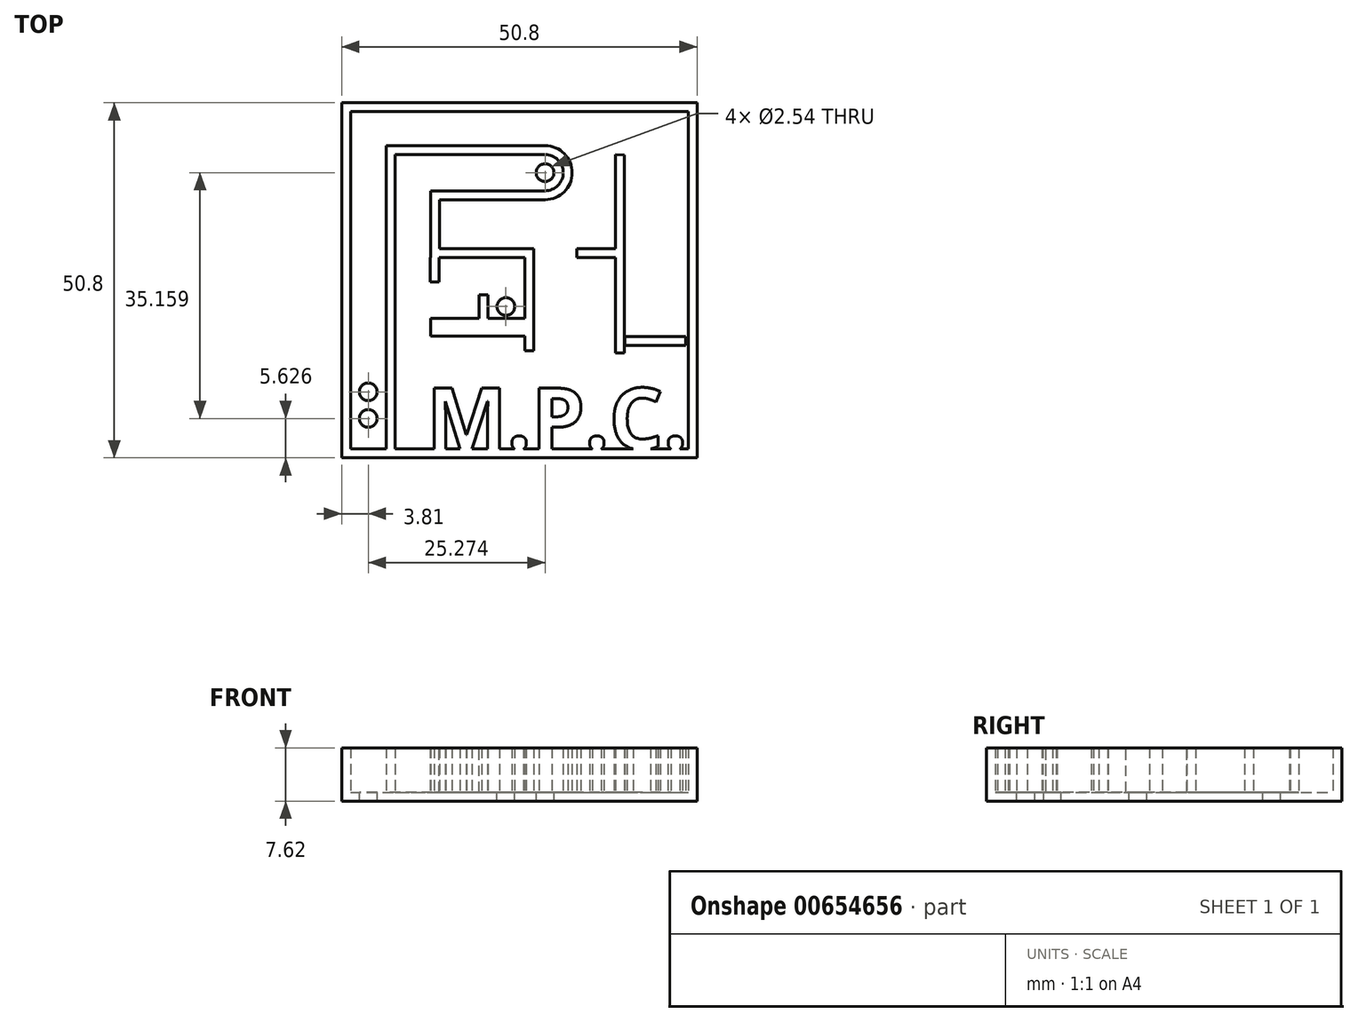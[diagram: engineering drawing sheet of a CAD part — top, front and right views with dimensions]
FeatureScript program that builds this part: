
annotation { "Feature Type Name" : "Feature", "Feature Type Description" : "" }
export const myFeature = defineFeature(function(context is Context, id is Id, definition is map)
    precondition{}
    {
        {
            var Q0;
            Q0=qCreatedBy(makeId("Top.planeOp"),FACE);
            var sketch = newSketch(context, id + "F0", { "sketchPlane" : qUnion([Q0])});
            skLineSegment(sketch, "E0.bottom", {"start": v(0, 0) * mm, "end": v(50.8, 0) * mm});
            skLineSegment(sketch, "E0.top", {"start": v(0, 50.8) * mm, "end": v(50.8, 50.8) * mm});
            skLineSegment(sketch, "E0.left", {"start": v(0, 0) * mm, "end": v(0, 50.8) * mm});
            skLineSegment(sketch, "E0.right", {"start": v(50.8, 0) * mm, "end": v(50.8, 50.8) * mm});
            skSolve(sketch);
        }
        {
            var Q0;
            Q0 = qSketchRegion(id + "F0", true);
            extrude(context, id + "F1", {"entities" : qUnion([Q0]), "depth" : 7.62 * mm, "offsetDistance" : 25.4 * mm});
        }
        {
            var Q0;
            Q0=makeQuery(id+"F1.opExtrude","CAP_FACE",FACE,{"disambiguationData":[OSD([sQuery(id+"F0.wireOp",EDGE,"E0.bottom"),sQuery(id+"F0.wireOp",EDGE,"E0.top"),sQuery(id+"F0.wireOp",EDGE,"E0.left"),sQuery(id+"F0.wireOp",EDGE,"E0.right")])],"isStart":false});
            shell(context, id + "F2", {"entities" : qUnion([Q0]), "thickness" : 1.27 * mm});
        }
        {
            var Q0;
            Q0=makeQuery(id+"F2.opShell","OFFSET_FACE",FACE,{"disambiguationData":[OSD([sQuery(id+"F0.wireOp",EDGE,"E0.bottom"),sQuery(id+"F0.wireOp",EDGE,"E0.top"),sQuery(id+"F0.wireOp",EDGE,"E0.left"),sQuery(id+"F0.wireOp",EDGE,"E0.right")])]});
            var sketch = newSketch(context, id + "F3", { "sketchPlane" : qUnion([Q0])});
            skLineSegment(sketch, "E1", {"start": v(1.27, 5.76) * mm, "end": v(6.35, 5.76) * mm});
            skLineSegment(sketch, "E2", {"start": v(6.35, 5.76) * mm, "end": v(6.35, 1.27) * mm});
            skLineSegment(sketch, "E3", {"start": v(6.35, 1.27) * mm, "end": v(7.62, 1.27) * mm});
            skLineSegment(sketch, "E4", {"start": v(7.62, 1.27) * mm, "end": v(7.62, 44.65) * mm});
            skLineSegment(sketch, "E5", {"start": v(7.62, 44.65) * mm, "end": v(6.35, 44.65) * mm});
            skLineSegment(sketch, "E6", {"start": v(6.35, 44.65) * mm, "end": v(6.35, 5.76) * mm});
            skSolve(sketch);
        }
        {
            var Q0;
            Q0=makeQuery(id+"F3.imprint","IMPRINT",FACE,{"disambiguationData":[TD([[makeQuery(id+"F3.imprint","IMPRINT",EDGE,{"derivedFrom":sQuery(id+"F3.wireOp",EDGE,"E2")}),1.0]])]});
            extrude(context, id + "F4", {"entities" : qUnion([Q0]), "operationType" : NewBodyOperationType.ADD, "depth" : 6.35 * mm, "offsetDistance" : 25.4 * mm});
        }
        {
            var Q0;
            Q0=makeQuery(id+"F2.opShell","OFFSET_FACE",FACE,{"disambiguationData":[OSD([sQuery(id+"F0.wireOp",EDGE,"E0.bottom"),sQuery(id+"F0.wireOp",EDGE,"E0.top"),sQuery(id+"F0.wireOp",EDGE,"E0.left"),sQuery(id+"F0.wireOp",EDGE,"E0.right")])]});
            var sketch = newSketch(context, id + "F5", { "sketchPlane" : qUnion([Q0])});
            skText(sketch, "E7", { "text": "M.P.C.", "fontName": "OpenSans-Bold.ttf"});
            const initialGuessF5  = {"E7": [0.01217, 0.00127, 1, 0, 0.00876]};
            skSetInitialGuess(sketch, initialGuessF5);
            skSolve(sketch);
        }
        {
            var Q0;
            Q0 = qSketchRegion(id + "F5", true);
            extrude(context, id + "F6", {"entities" : qUnion([Q0]), "operationType" : NewBodyOperationType.ADD, "depth" : 6.35 * mm, "offsetDistance" : 25.4 * mm});
        }
        {
            var Q0;
            {var subQ0=sQuery(id+"F0.wireOp",EDGE,"E0.top");var subQ1=sQuery(id+"F0.wireOp",EDGE,"E0.bottom");var subQ2=sQuery(id+"F0.wireOp",EDGE,"E0.right");var subQ3=sQuery(id+"F0.wireOp",EDGE,"E0.left");Q0=makeQuery(id+"F6.boolean.opBoolean","SPLIT",FACE,{"disambiguationData":[TD([makeQuery(id+"F2.opShell","OFFSET_FACE",FACE,{"disambiguationData":[OSD([subQ0])]})])],"derivedFrom":makeQuery(id+"F2.opShell","OFFSET_FACE",FACE,{"disambiguationData":[OSD([subQ1,subQ0,subQ3,subQ2])]})});}
            var sketch = newSketch(context, id + "F7", { "sketchPlane" : qUnion([Q0])});
            skCircle(sketch, "E8", {"center": v(3.81, 5.63) * mm, "radius": 1.27 * mm});
            skSolve(sketch);
        }
        {
            var Q0;
            Q0=makeQuery(id+"F7.imprint","IMPRINT",FACE,{"disambiguationData":[TD([[makeQuery(id+"F7.imprint","IMPRINT",EDGE,{"derivedFrom":sQuery(id+"F7.wireOp",EDGE,"E8")}),1.0]])]});
            extrude(context, id + "F8", {"entities" : qUnion([Q0]), "operationType" : NewBodyOperationType.REMOVE, "oppositeDirection" : true, "depth" : 7.62 * mm, "offsetDistance" : 25.4 * mm});
        }
        {
            var Q0;
            {var subQ0=sQuery(id+"F0.wireOp",EDGE,"E0.top");var subQ1=sQuery(id+"F0.wireOp",EDGE,"E0.bottom");var subQ2=sQuery(id+"F0.wireOp",EDGE,"E0.right");var subQ3=sQuery(id+"F0.wireOp",EDGE,"E0.left");Q0=makeQuery(id+"F6.boolean.opBoolean","SPLIT",FACE,{"disambiguationData":[TD([makeQuery(id+"F2.opShell","OFFSET_FACE",FACE,{"disambiguationData":[OSD([subQ0])]})])],"derivedFrom":makeQuery(id+"F2.opShell","OFFSET_FACE",FACE,{"disambiguationData":[OSD([subQ1,subQ0,subQ3,subQ2])]})});}
            var sketch = newSketch(context, id + "F9", { "sketchPlane" : qUnion([Q0])});
            skCircle(sketch, "E9", {"center": v(3.81, 9.44) * mm, "radius": 1.27 * mm});
            skSolve(sketch);
        }
        {
            var Q0;
            Q0=makeQuery(id+"F9.imprint","IMPRINT",FACE,{"disambiguationData":[TD([[makeQuery(id+"F9.imprint","IMPRINT",EDGE,{"derivedFrom":sQuery(id+"F9.wireOp",EDGE,"E9")}),1.0]])]});
            extrude(context, id + "F10", {"entities" : qUnion([Q0]), "operationType" : NewBodyOperationType.REMOVE, "oppositeDirection" : true, "depth" : 7.62 * mm, "offsetDistance" : 25.4 * mm});
        }
        {
            var Q0;
            {var subQ0=sQuery(id+"F0.wireOp",EDGE,"E0.top");var subQ1=sQuery(id+"F0.wireOp",EDGE,"E0.bottom");var subQ2=sQuery(id+"F0.wireOp",EDGE,"E0.right");var subQ3=sQuery(id+"F0.wireOp",EDGE,"E0.left");Q0=makeQuery(id+"F6.boolean.opBoolean","SPLIT",FACE,{"disambiguationData":[TD([makeQuery(id+"F2.opShell","OFFSET_FACE",FACE,{"disambiguationData":[OSD([subQ0])]})])],"derivedFrom":makeQuery(id+"F2.opShell","OFFSET_FACE",FACE,{"disambiguationData":[OSD([subQ1,subQ0,subQ3,subQ2])]})});}
            var sketch = newSketch(context, id + "F11", { "sketchPlane" : qUnion([Q0])});
            skLineSegment(sketch, "E10", {"start": v(7.62, 44.65) * mm, "end": v(29.08, 44.65) * mm});
            skLineSegment(sketch, "E11", {"start": v(29.08, 44.65) * mm, "end": v(29.08, 43.38) * mm});
            skLineSegment(sketch, "E12", {"start": v(29.08, 43.38) * mm, "end": v(7.62, 43.38) * mm});
            skLineSegment(sketch, "E13", {"start": v(7.62, 43.38) * mm, "end": v(7.62, 44.65) * mm});
            skArc(sketch, "E14", {"start": v(29.08, 38.2) * mm, "mid": v(31.68, 40.78) * mm, "end": v(29.08, 43.38) * mm});
            skLineSegment(sketch, "E15", {"start": v(29.08, 38.2) * mm, "end": v(29.08, 36.92) * mm});
            skArc(sketch, "E16", {"start": v(29.08, 36.92) * mm, "mid": v(32.95, 40.78) * mm, "end": v(29.08, 44.65) * mm});
            skSolve(sketch);
        }
        {
            var Q0;
            Q0 = qSketchRegion(id + "F11", true);
            extrude(context, id + "F12", {"entities" : qUnion([Q0]), "operationType" : NewBodyOperationType.ADD, "depth" : 6.35 * mm, "offsetDistance" : 25.4 * mm});
        }
        {
            var Q0;
            {var subQ0=sQuery(id+"F0.wireOp",EDGE,"E0.top");var subQ1=sQuery(id+"F0.wireOp",EDGE,"E0.bottom");var subQ2=sQuery(id+"F0.wireOp",EDGE,"E0.right");var subQ3=sQuery(id+"F0.wireOp",EDGE,"E0.left");Q0=makeQuery(id+"F6.boolean.opBoolean","SPLIT",FACE,{"disambiguationData":[TD([makeQuery(id+"F2.opShell","OFFSET_FACE",FACE,{"disambiguationData":[OSD([subQ0])]})])],"derivedFrom":makeQuery(id+"F2.opShell","OFFSET_FACE",FACE,{"disambiguationData":[OSD([subQ1,subQ0,subQ3,subQ2])]})});}
            var sketch = newSketch(context, id + "F13", { "sketchPlane" : qUnion([Q0])});
            skLineSegment(sketch, "E17", {"start": v(29.08, 38.2) * mm, "end": v(12.7, 38.2) * mm});
            skLineSegment(sketch, "E18", {"start": v(12.7, 38.2) * mm, "end": v(12.7, 36.92) * mm});
            skLineSegment(sketch, "E19", {"start": v(12.7, 36.92) * mm, "end": v(29.08, 36.92) * mm});
            skLineSegment(sketch, "E20", {"start": v(29.08, 36.92) * mm, "end": v(29.08, 38.2) * mm});
            skLineSegment(sketch, "E21", {"start": v(14.01, 38.2) * mm, "end": v(14.01, 38.3) * mm});
            skLineSegment(sketch, "E22", {"start": v(14.01, 38.3) * mm, "end": v(15.18, 38.3) * mm});
            skLineSegment(sketch, "E23", {"start": v(15.18, 38.3) * mm, "end": v(15.18, 38.2) * mm});
            skLineSegment(sketch, "E24", {"start": v(15.18, 38.2) * mm, "end": v(14.01, 38.2) * mm});
            skSolve(sketch);
        }
        {
            var Q0;
            {var subQ0=sQuery(id+"F13.wireOp",EDGE,"E18");Q0=makeQuery(id+"F13.imprint","IMPRINT",FACE,{"disambiguationData":[TD([[makeQuery(id+"F13.imprint","IMPRINT",EDGE,{"derivedFrom":subQ0}),1.0]])]});}
            extrude(context, id + "F14", {"entities" : qUnion([Q0]), "operationType" : NewBodyOperationType.ADD, "depth" : 6.35 * mm, "offsetDistance" : 25.4 * mm});
        }
        {
            var Q0;
            {var subQ0=sQuery(id+"F0.wireOp",EDGE,"E0.top");var subQ1=sQuery(id+"F0.wireOp",EDGE,"E0.bottom");var subQ2=sQuery(id+"F0.wireOp",EDGE,"E0.right");var subQ3=sQuery(id+"F0.wireOp",EDGE,"E0.left");Q0=makeQuery(id+"F6.boolean.opBoolean","SPLIT",FACE,{"disambiguationData":[TD([makeQuery(id+"F2.opShell","OFFSET_FACE",FACE,{"disambiguationData":[OSD([subQ0])]})])],"derivedFrom":makeQuery(id+"F2.opShell","OFFSET_FACE",FACE,{"disambiguationData":[OSD([subQ1,subQ0,subQ3,subQ2])]})});}
            var sketch = newSketch(context, id + "F15", { "sketchPlane" : qUnion([Q0])});
            skCircle(sketch, "E25", {"center": v(29.08, 40.78) * mm, "radius": 1.27 * mm});
            skSolve(sketch);
        }
        {
            var Q0;
            Q0=makeQuery(id+"F15.imprint","IMPRINT",FACE,{"disambiguationData":[TD([[makeQuery(id+"F15.imprint","IMPRINT",EDGE,{"derivedFrom":sQuery(id+"F15.wireOp",EDGE,"E25")}),1.0]])]});
            extrude(context, id + "F16", {"entities" : qUnion([Q0]), "operationType" : NewBodyOperationType.REMOVE, "oppositeDirection" : true, "depth" : 7.62 * mm, "offsetDistance" : 25.4 * mm});
        }
        {
            var Q0;
            {var subQ0=sQuery(id+"F0.wireOp",EDGE,"E0.top");var subQ1=sQuery(id+"F0.wireOp",EDGE,"E0.bottom");var subQ2=sQuery(id+"F0.wireOp",EDGE,"E0.right");var subQ3=sQuery(id+"F0.wireOp",EDGE,"E0.left");Q0=makeQuery(id+"F6.boolean.opBoolean","SPLIT",FACE,{"disambiguationData":[TD([makeQuery(id+"F2.opShell","OFFSET_FACE",FACE,{"disambiguationData":[OSD([subQ0])]})])],"derivedFrom":makeQuery(id+"F2.opShell","OFFSET_FACE",FACE,{"disambiguationData":[OSD([subQ1,subQ0,subQ3,subQ2])]})});}
            var sketch = newSketch(context, id + "F17", { "sketchPlane" : qUnion([Q0])});
            skLineSegment(sketch, "E26", {"start": v(12.7, 36.92) * mm, "end": v(12.7, 28.66) * mm});
            skLineSegment(sketch, "E27", {"start": v(12.7, 28.66) * mm, "end": v(13.97, 28.66) * mm});
            skLineSegment(sketch, "E28", {"start": v(13.97, 28.66) * mm, "end": v(13.97, 36.92) * mm});
            skLineSegment(sketch, "E29", {"start": v(13.97, 36.92) * mm, "end": v(12.7, 36.92) * mm});
            skLineSegment(sketch, "E30", {"start": v(13.97, 28.66) * mm, "end": v(27.44, 28.66) * mm});
            skLineSegment(sketch, "E31", {"start": v(27.44, 28.66) * mm, "end": v(27.44, 29.94) * mm});
            skLineSegment(sketch, "E32", {"start": v(27.44, 29.94) * mm, "end": v(13.97, 29.94) * mm});
            skLineSegment(sketch, "E33", {"start": v(13.97, 29.94) * mm, "end": v(13.97, 28.66) * mm});
            skLineSegment(sketch, "E34", {"start": v(27.44, 28.66) * mm, "end": v(27.44, 18.66) * mm});
            skLineSegment(sketch, "E35", {"start": v(27.44, 18.66) * mm, "end": v(26.17, 18.66) * mm});
            skLineSegment(sketch, "E36", {"start": v(26.17, 18.66) * mm, "end": v(26.17, 28.66) * mm});
            skLineSegment(sketch, "E37", {"start": v(26.17, 28.66) * mm, "end": v(27.44, 28.66) * mm});
            skLineSegment(sketch, "E38", {"start": v(26.17, 18.66) * mm, "end": v(12.7, 18.66) * mm});
            skLineSegment(sketch, "E39", {"start": v(12.7, 18.66) * mm, "end": v(12.7, 19.93) * mm});
            skLineSegment(sketch, "E40", {"start": v(12.7, 19.93) * mm, "end": v(26.17, 19.93) * mm});
            skLineSegment(sketch, "E41", {"start": v(26.17, 19.93) * mm, "end": v(26.17, 18.66) * mm});
            skSolve(sketch);
        }
        {
            var Q0;
            Q0=makeQuery(id+"F17.imprint","IMPRINT",FACE,{"disambiguationData":[TD([[makeQuery(id+"F17.imprint","IMPRINT",EDGE,{"derivedFrom":sQuery(id+"F17.wireOp",EDGE,"E30")}),1.0]])]});
            var Q1;
            Q1=makeQuery(id+"F17.imprint","IMPRINT",FACE,{"disambiguationData":[TD([[makeQuery(id+"F17.imprint","IMPRINT",EDGE,{"derivedFrom":sQuery(id+"F17.wireOp",EDGE,"E26")}),1.0]])]});
            var Q2;
            Q2=makeQuery(id+"F17.imprint","IMPRINT",FACE,{"disambiguationData":[TD([[makeQuery(id+"F17.imprint","IMPRINT",EDGE,{"derivedFrom":sQuery(id+"F17.wireOp",EDGE,"E34")}),-1.0]])]});
            var Q3;
            Q3=makeQuery(id+"F17.imprint","IMPRINT",FACE,{"disambiguationData":[TD([[makeQuery(id+"F17.imprint","IMPRINT",EDGE,{"derivedFrom":sQuery(id+"F17.wireOp",EDGE,"E38")}),-1.0]])]});
            extrude(context, id + "F18", {"entities" : qUnion([Q0, Q1, Q2, Q3]), "operationType" : NewBodyOperationType.ADD, "depth" : 6.35 * mm, "offsetDistance" : 25.4 * mm});
        }
        {
            var Q0;
            {var subQ0=sQuery(id+"F0.wireOp",EDGE,"E0.top");var subQ1=sQuery(id+"F0.wireOp",EDGE,"E0.bottom");var subQ2=sQuery(id+"F0.wireOp",EDGE,"E0.right");var subQ3=sQuery(id+"F0.wireOp",EDGE,"E0.left");Q0=makeQuery(id+"F6.boolean.opBoolean","SPLIT",FACE,{"disambiguationData":[TD([makeQuery(id+"F2.opShell","OFFSET_FACE",FACE,{"disambiguationData":[OSD([subQ0])]})])],"derivedFrom":makeQuery(id+"F2.opShell","OFFSET_FACE",FACE,{"disambiguationData":[OSD([subQ1,subQ0,subQ3,subQ2])]})});}
            var sketch = newSketch(context, id + "F19", { "sketchPlane" : qUnion([Q0])});
            skLineSegment(sketch, "E42", {"start": v(39.17, 43.4) * mm, "end": v(39.17, 15.02) * mm});
            skLineSegment(sketch, "E43", {"start": v(39.17, 15.02) * mm, "end": v(40.44, 15.02) * mm});
            skLineSegment(sketch, "E44", {"start": v(40.44, 15.02) * mm, "end": v(40.44, 43.3) * mm});
            skLineSegment(sketch, "E45", {"start": v(40.44, 43.3) * mm, "end": v(39.17, 43.4) * mm});
            skLineSegment(sketch, "E46", {"start": v(39.17, 29.93) * mm, "end": v(33.64, 29.93) * mm});
            skLineSegment(sketch, "E47", {"start": v(33.64, 29.93) * mm, "end": v(33.64, 28.66) * mm});
            skLineSegment(sketch, "E48", {"start": v(33.64, 28.66) * mm, "end": v(39.17, 28.66) * mm});
            skLineSegment(sketch, "E49", {"start": v(39.17, 28.66) * mm, "end": v(39.17, 29.93) * mm});
            skLineSegment(sketch, "E50", {"start": v(27.44, 18.66) * mm, "end": v(27.44, 17.4) * mm});
            skLineSegment(sketch, "E51", {"start": v(27.44, 17.4) * mm, "end": v(12.7, 17.4) * mm});
            skLineSegment(sketch, "E52", {"start": v(12.7, 17.4) * mm, "end": v(12.7, 18.66) * mm});
            skLineSegment(sketch, "E53", {"start": v(12.7, 18.66) * mm, "end": v(27.44, 18.66) * mm});
            skLineSegment(sketch, "E54", {"start": v(27.44, 17.4) * mm, "end": v(27.44, 15.33) * mm});
            skLineSegment(sketch, "E55", {"start": v(27.44, 15.33) * mm, "end": v(26.17, 15.33) * mm});
            skLineSegment(sketch, "E56", {"start": v(26.17, 15.33) * mm, "end": v(26.17, 17.4) * mm});
            skLineSegment(sketch, "E57", {"start": v(26.17, 17.4) * mm, "end": v(27.44, 17.4) * mm});
            skSolve(sketch);
        }
        {
            var Q0;
            Q0=makeQuery(id+"F19.imprint","IMPRINT",FACE,{"disambiguationData":[TD([[makeQuery(id+"F19.imprint","IMPRINT",EDGE,{"derivedFrom":sQuery(id+"F19.wireOp",EDGE,"E46")}),1.0]])]});
            var Q1;
            {var subQ0=sQuery(id+"F19.wireOp",EDGE,"E43");Q1=makeQuery(id+"F19.imprint","IMPRINT",FACE,{"disambiguationData":[TD([[makeQuery(id+"F19.imprint","IMPRINT",EDGE,{"derivedFrom":subQ0}),1.0]])]});}
            var Q2;
            Q2=makeQuery(id+"F19.imprint","IMPRINT",FACE,{"disambiguationData":[TD([[makeQuery(id+"F19.imprint","IMPRINT",EDGE,{"derivedFrom":sQuery(id+"F19.wireOp",EDGE,"E50")}),-1.0]])]});
            var Q3;
            Q3=makeQuery(id+"F19.imprint","IMPRINT",FACE,{"disambiguationData":[TD([[makeQuery(id+"F19.imprint","IMPRINT",EDGE,{"derivedFrom":sQuery(id+"F19.wireOp",EDGE,"E54")}),-1.0]])]});
            extrude(context, id + "F20", {"entities" : qUnion([Q0, Q1, Q2, Q3]), "operationType" : NewBodyOperationType.ADD, "depth" : 6.35 * mm, "offsetDistance" : 25.4 * mm});
        }
        {
            var Q0;
            {var subQ0=sQuery(id+"F0.wireOp",EDGE,"E0.top");var subQ1=sQuery(id+"F0.wireOp",EDGE,"E0.bottom");var subQ2=sQuery(id+"F0.wireOp",EDGE,"E0.right");var subQ3=sQuery(id+"F0.wireOp",EDGE,"E0.left");Q0=makeQuery(id+"F6.boolean.opBoolean","SPLIT",FACE,{"disambiguationData":[TD([makeQuery(id+"F2.opShell","OFFSET_FACE",FACE,{"disambiguationData":[OSD([subQ0])]})])],"derivedFrom":makeQuery(id+"F2.opShell","OFFSET_FACE",FACE,{"disambiguationData":[OSD([subQ1,subQ0,subQ3,subQ2])]})});}
            var sketch = newSketch(context, id + "F21", { "sketchPlane" : qUnion([Q0])});
            skSolve(sketch);
        }
        {
            var Q0;
            {var subQ6=sQuery(id+"F5.wireOp",EDGE,"E7.sketch_text.stroke-5");Q0=makeQuery(id+"F21.imprint","IMPRINT",FACE,{"disambiguationData":[TD([[makeQuery(id+"F21.imprint","IMPRINT",EDGE,{"derivedFrom":makeQuery(id+"F6.opExtrude","CAP_EDGE",EDGE,{"disambiguationData":[OSD([subQ6])],"isStart":true})}),1.0]])]});}
            var sketch = newSketch(context, id + "F22", { "sketchPlane" : qUnion([Q0])});
            skLineSegment(sketch, "E58", {"start": v(12.65, 28.66) * mm, "end": v(12.65, 25.15) * mm});
            skLineSegment(sketch, "E59", {"start": v(12.65, 25.15) * mm, "end": v(13.92, 25.15) * mm});
            skLineSegment(sketch, "E60", {"start": v(13.92, 25.15) * mm, "end": v(13.92, 28.66) * mm});
            skLineSegment(sketch, "E61", {"start": v(13.92, 28.66) * mm, "end": v(12.65, 28.66) * mm});
            skLineSegment(sketch, "E62", {"start": v(19.67, 19.94) * mm, "end": v(19.67, 23.34) * mm});
            skLineSegment(sketch, "E63", {"start": v(19.67, 23.34) * mm, "end": v(20.95, 23.34) * mm});
            skLineSegment(sketch, "E64", {"start": v(20.95, 23.34) * mm, "end": v(20.95, 19.94) * mm});
            skLineSegment(sketch, "E65", {"start": v(20.95, 19.94) * mm, "end": v(19.67, 19.94) * mm});
            skSolve(sketch);
        }
        {
            var Q0;
            Q0 = qSketchRegion(id + "F22", true);
            extrude(context, id + "F23", {"entities" : qUnion([Q0]), "operationType" : NewBodyOperationType.ADD, "depth" : 6.35 * mm, "offsetDistance" : 25.4 * mm});
        }
        {
            var Q0;
            {var subQ6=sQuery(id+"F5.wireOp",EDGE,"E7.sketch_text.stroke-5");Q0=makeQuery(id+"F21.imprint","IMPRINT",FACE,{"disambiguationData":[TD([[makeQuery(id+"F21.imprint","IMPRINT",EDGE,{"derivedFrom":makeQuery(id+"F6.opExtrude","CAP_EDGE",EDGE,{"disambiguationData":[OSD([subQ6])],"isStart":true})}),1.0]])]});}
            var sketch = newSketch(context, id + "F24", { "sketchPlane" : qUnion([Q0])});
            skCircle(sketch, "E66", {"center": v(23.49, 21.64) * mm, "radius": 1.27 * mm});
            skSolve(sketch);
        }
        {
            var Q0;
            Q0 = qSketchRegion(id + "F24", true);
            extrude(context, id + "F25", {"entities" : qUnion([Q0]), "operationType" : NewBodyOperationType.REMOVE, "oppositeDirection" : true, "depth" : 7.62 * mm, "offsetDistance" : 25.4 * mm});
        }
        {
            var Q0;
            {var subQ6=sQuery(id+"F5.wireOp",EDGE,"E7.sketch_text.stroke-5");Q0=makeQuery(id+"F21.imprint","IMPRINT",FACE,{"disambiguationData":[TD([[makeQuery(id+"F21.imprint","IMPRINT",EDGE,{"derivedFrom":makeQuery(id+"F6.opExtrude","CAP_EDGE",EDGE,{"disambiguationData":[OSD([subQ6])],"isStart":true})}),1.0]])]});}
            var sketch = newSketch(context, id + "F26", { "sketchPlane" : qUnion([Q0])});
            skLineSegment(sketch, "E67", {"start": v(40.49, 16.07) * mm, "end": v(49.2, 16.07) * mm});
            skLineSegment(sketch, "E68", {"start": v(49.2, 16.07) * mm, "end": v(49.2, 17.34) * mm});
            skLineSegment(sketch, "E69", {"start": v(49.2, 17.34) * mm, "end": v(40.49, 17.34) * mm});
            skLineSegment(sketch, "E70", {"start": v(40.49, 17.34) * mm, "end": v(40.49, 16.07) * mm});
            skSolve(sketch);
        }
        {
            var Q0;
            Q0 = qSketchRegion(id + "F26", true);
            extrude(context, id + "F27", {"entities" : qUnion([Q0]), "operationType" : NewBodyOperationType.ADD, "depth" : 6.35 * mm, "offsetDistance" : 25.4 * mm});
        }
    });
